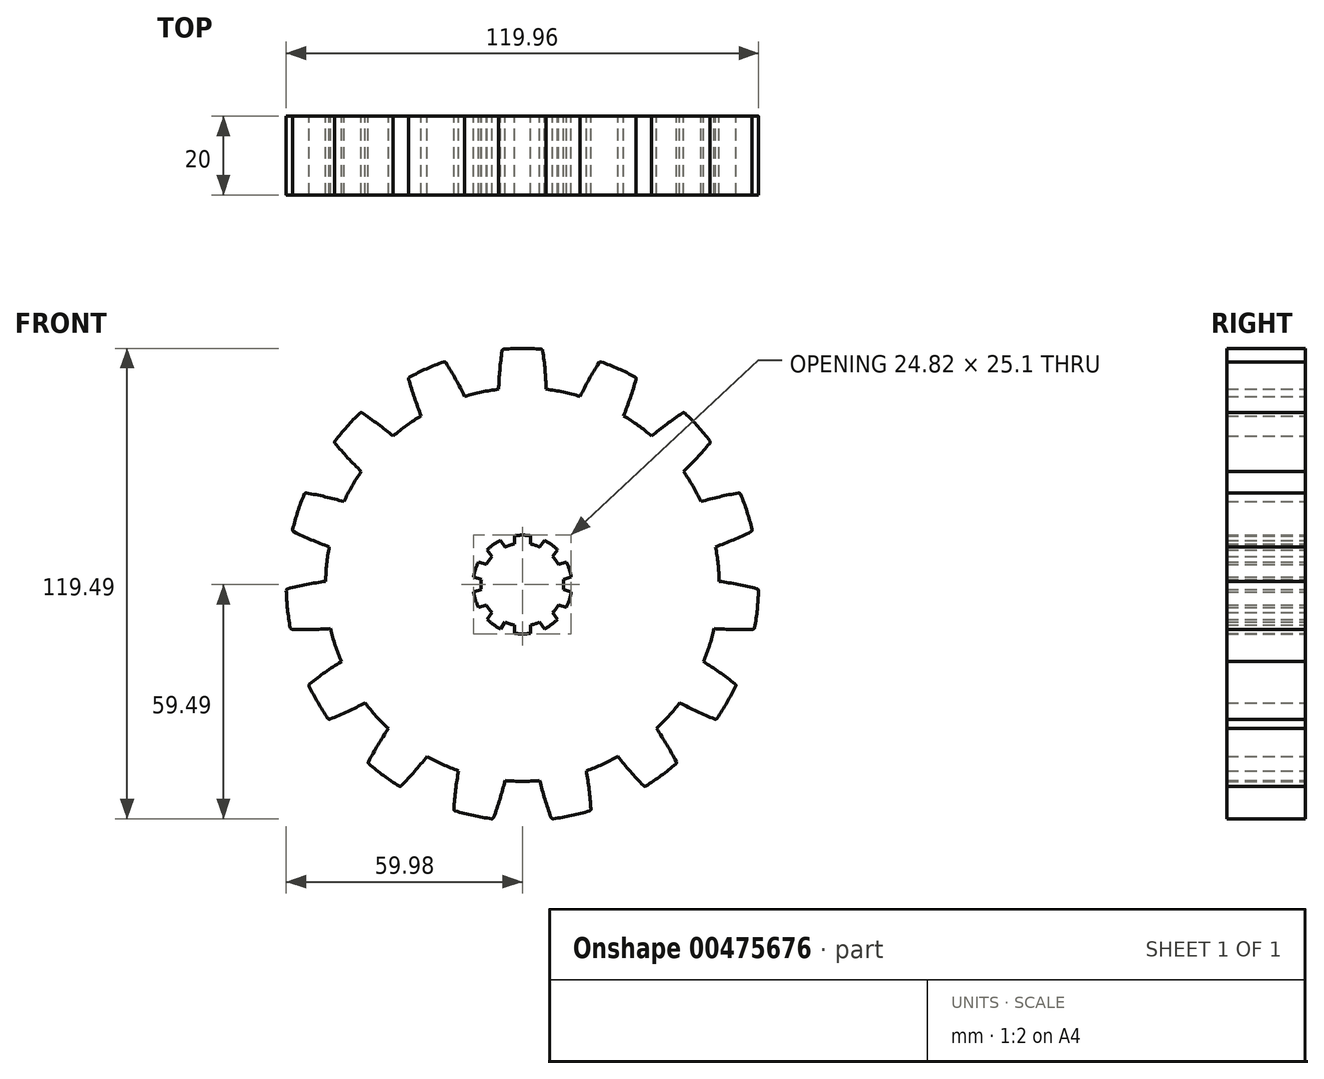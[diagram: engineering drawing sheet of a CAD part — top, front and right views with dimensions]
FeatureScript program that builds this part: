
annotation { "Feature Type Name" : "Feature", "Feature Type Description" : "" }
export const myFeature = defineFeature(function(context is Context, id is Id, definition is map)
    precondition{}
    {
        {
            var Q0;
            Q0=qCreatedBy(makeId("Front.planeOp"),FACE);
            var sketch = newSketch(context, id + "F0", { "sketchPlane" : qUnion([Q0])});
            skArc(sketch, "E0", {"start": v(2.05, 12.38) * mm, "mid": v(0, 12.55) * mm, "end": v(-2.05, 12.38) * mm});
            skArc(sketch, "E1", {"start": v(-10.43, 1.23) * mm, "mid": v(-10.5, 0) * mm, "end": v(-10.43, -1.23) * mm});
            skLineSegment(sketch, "E2.left", {"start": v(2.05, 12.38) * mm, "end": v(2.05, 10.3) * mm});
            skLineSegment(sketch, "E2.right", {"start": v(-2.05, 12.38) * mm, "end": v(-2.05, 10.3) * mm});
            skPoint(sketch, "E3.orphan", {"position": v(-2.05, 12.55) * mm});
            skPoint(sketch, "E4.orphan", {"position": v(2.05, 12.55) * mm});
            skPoint(sketch, "E5.trimOffspring.end.orphan", {"position": v(2.05, -12.55) * mm});
            skPoint(sketch, "E6.trimOffspring.end.orphan", {"position": v(-2.05, -12.55) * mm});
            skLineSegment(sketch, "E7.1.0", {"start": v(-8.94, 8.81) * mm, "end": v(-7.71, 7.13) * mm});
            skArc(sketch, "E7.1.1", {"start": v(-5.62, 11.22) * mm, "mid": v(-7.38, 10.15) * mm, "end": v(-8.94, 8.81) * mm});
            skLineSegment(sketch, "E7.1.2", {"start": v(-5.62, 11.22) * mm, "end": v(-4.4, 9.54) * mm});
            skLineSegment(sketch, "E7.2.0", {"start": v(-12.4, 1.88) * mm, "end": v(-10.43, 1.23) * mm});
            skArc(sketch, "E7.2.1", {"start": v(-11.14, 5.78) * mm, "mid": v(-11.94, 3.88) * mm, "end": v(-12.4, 1.88) * mm});
            skLineSegment(sketch, "E7.2.2", {"start": v(-11.14, 5.78) * mm, "end": v(-9.16, 5.13) * mm});
            skLineSegment(sketch, "E7.3.0", {"start": v(-11.14, -5.78) * mm, "end": v(-9.16, -5.13) * mm});
            skArc(sketch, "E7.3.1", {"start": v(-12.4, -1.88) * mm, "mid": v(-11.94, -3.88) * mm, "end": v(-11.14, -5.78) * mm});
            skLineSegment(sketch, "E7.3.2", {"start": v(-12.4, -1.88) * mm, "end": v(-10.43, -1.23) * mm});
            skLineSegment(sketch, "E7.4.0", {"start": v(-5.62, -11.22) * mm, "end": v(-4.4, -9.54) * mm});
            skArc(sketch, "E7.4.1", {"start": v(-8.94, -8.81) * mm, "mid": v(-7.38, -10.15) * mm, "end": v(-5.62, -11.22) * mm});
            skLineSegment(sketch, "E7.4.2", {"start": v(-8.94, -8.81) * mm, "end": v(-7.71, -7.13) * mm});
            skLineSegment(sketch, "E7.5.0", {"start": v(2.05, -12.38) * mm, "end": v(2.05, -10.3) * mm});
            skArc(sketch, "E7.5.1", {"start": v(-2.05, -12.38) * mm, "mid": v(0, -12.55) * mm, "end": v(2.05, -12.38) * mm});
            skLineSegment(sketch, "E7.5.2", {"start": v(-2.05, -12.38) * mm, "end": v(-2.05, -10.3) * mm});
            skLineSegment(sketch, "E7.6.0", {"start": v(8.94, -8.81) * mm, "end": v(7.71, -7.13) * mm});
            skArc(sketch, "E7.6.1", {"start": v(5.62, -11.22) * mm, "mid": v(7.38, -10.15) * mm, "end": v(8.94, -8.81) * mm});
            skLineSegment(sketch, "E7.6.2", {"start": v(5.62, -11.22) * mm, "end": v(4.4, -9.54) * mm});
            skLineSegment(sketch, "E7.7.0", {"start": v(12.4, -1.88) * mm, "end": v(10.43, -1.23) * mm});
            skArc(sketch, "E7.7.1", {"start": v(11.14, -5.78) * mm, "mid": v(11.94, -3.88) * mm, "end": v(12.4, -1.88) * mm});
            skLineSegment(sketch, "E7.7.2", {"start": v(11.14, -5.78) * mm, "end": v(9.16, -5.13) * mm});
            skLineSegment(sketch, "E7.8.0", {"start": v(11.14, 5.78) * mm, "end": v(9.16, 5.13) * mm});
            skArc(sketch, "E7.8.1", {"start": v(12.4, 1.88) * mm, "mid": v(11.94, 3.88) * mm, "end": v(11.14, 5.78) * mm});
            skLineSegment(sketch, "E7.8.2", {"start": v(12.4, 1.88) * mm, "end": v(10.43, 1.23) * mm});
            skLineSegment(sketch, "E7.9.0", {"start": v(5.62, 11.22) * mm, "end": v(4.4, 9.54) * mm});
            skArc(sketch, "E7.9.1", {"start": v(8.94, 8.81) * mm, "mid": v(7.38, 10.15) * mm, "end": v(5.62, 11.22) * mm});
            skLineSegment(sketch, "E7.9.2", {"start": v(8.94, 8.81) * mm, "end": v(7.71, 7.13) * mm});
            skArc(sketch, "E8.trimOffspring", {"start": v(-7.71, 7.13) * mm, "mid": v(-8.5, 6.17) * mm, "end": v(-9.16, 5.13) * mm});
            skArc(sketch, "E9.trimOffspring", {"start": v(-2.05, 10.3) * mm, "mid": v(-3.24, 9.99) * mm, "end": v(-4.4, 9.54) * mm});
            skArc(sketch, "E10.trimOffspring", {"start": v(4.4, 9.54) * mm, "mid": v(3.24, 9.99) * mm, "end": v(2.05, 10.3) * mm});
            skArc(sketch, "E11.trimOffspring", {"start": v(9.16, 5.13) * mm, "mid": v(8.5, 6.17) * mm, "end": v(7.71, 7.13) * mm});
            skArc(sketch, "E12.trimOffspring", {"start": v(10.43, -1.23) * mm, "mid": v(10.5, 0) * mm, "end": v(10.43, 1.23) * mm});
            skArc(sketch, "E13.trimOffspring", {"start": v(7.71, -7.13) * mm, "mid": v(8.5, -6.17) * mm, "end": v(9.16, -5.13) * mm});
            skArc(sketch, "E14.trimOffspring", {"start": v(2.05, -10.3) * mm, "mid": v(3.24, -9.99) * mm, "end": v(4.4, -9.54) * mm});
            skArc(sketch, "E15.trimOffspring", {"start": v(-4.4, -9.54) * mm, "mid": v(-3.24, -9.99) * mm, "end": v(-2.05, -10.3) * mm});
            skArc(sketch, "E16.trimOffspring", {"start": v(-9.16, -5.13) * mm, "mid": v(-8.5, -6.17) * mm, "end": v(-7.71, -7.13) * mm});
            skArc(sketch, "E17", {"start": v(-5.11, 59.78) * mm, "mid": v(-5.72, 54.72) * mm, "end": v(-6.05, 49.63) * mm});
            skArc(sketch, "E18.trimOffspring", {"start": v(5.11, 59.78) * mm, "mid": v(0, 60) * mm, "end": v(-5.11, 59.78) * mm});
            skArc(sketch, "E19.trimOffspring", {"start": v(6.05, 49.63) * mm, "mid": v(5.72, 54.72) * mm, "end": v(5.11, 59.78) * mm});
            skPoint(sketch, "E20.orphan", {"position": v(0, 46.5) * mm});
            skArc(sketch, "E21.1.0", {"start": v(-14.66, 47.8) * mm, "mid": v(-17.03, 52.32) * mm, "end": v(-19.64, 56.7) * mm});
            skPoint(sketch, "E21.1.1", {"position": v(-18.91, 42.48) * mm});
            skArc(sketch, "E21.1.2", {"start": v(-19.64, 56.7) * mm, "mid": v(-24.4, 54.81) * mm, "end": v(-28.99, 52.53) * mm});
            skArc(sketch, "E21.1.3", {"start": v(-28.99, 52.53) * mm, "mid": v(-27.49, 47.66) * mm, "end": v(-25.71, 42.88) * mm});
            skArc(sketch, "E21.2.0", {"start": v(-32.84, 37.7) * mm, "mid": v(-36.84, 40.87) * mm, "end": v(-41, 43.8) * mm});
            skPoint(sketch, "E21.2.1", {"position": v(-34.56, 31.11) * mm});
            skArc(sketch, "E21.2.2", {"start": v(-41, 43.8) * mm, "mid": v(-44.59, 40.15) * mm, "end": v(-47.85, 36.2) * mm});
            skArc(sketch, "E21.2.3", {"start": v(-47.85, 36.2) * mm, "mid": v(-44.5, 32.36) * mm, "end": v(-40.93, 28.72) * mm});
            skArc(sketch, "E21.3.0", {"start": v(-45.34, 21.09) * mm, "mid": v(-50.27, 22.35) * mm, "end": v(-55.28, 23.34) * mm});
            skPoint(sketch, "E21.3.1", {"position": v(-44.22, 14.37) * mm});
            skArc(sketch, "E21.3.2", {"start": v(-55.28, 23.34) * mm, "mid": v(-57.06, 18.54) * mm, "end": v(-58.44, 13.6) * mm});
            skArc(sketch, "E21.3.3", {"start": v(-58.44, 13.6) * mm, "mid": v(-53.81, 11.47) * mm, "end": v(-49.07, 9.59) * mm});
            skArc(sketch, "E21.4.0", {"start": v(-50, 0.82) * mm, "mid": v(-55.02, -0.03) * mm, "end": v(-59.99, -1.16) * mm});
            skPoint(sketch, "E21.4.1", {"position": v(-46.25, -4.86) * mm});
            skArc(sketch, "E21.4.2", {"start": v(-59.99, -1.16) * mm, "mid": v(-59.67, -6.27) * mm, "end": v(-58.92, -11.34) * mm});
            skArc(sketch, "E21.4.3", {"start": v(-58.92, -11.34) * mm, "mid": v(-53.82, -11.41) * mm, "end": v(-48.73, -11.2) * mm});
            skArc(sketch, "E21.5.0", {"start": v(-46, -19.58) * mm, "mid": v(-50.25, -22.4) * mm, "end": v(-54.33, -25.46) * mm});
            skPoint(sketch, "E21.5.1", {"position": v(-40.27, -23.25) * mm});
            skArc(sketch, "E21.5.2", {"start": v(-54.33, -25.46) * mm, "mid": v(-51.96, -30) * mm, "end": v(-49.22, -34.32) * mm});
            skArc(sketch, "E21.5.3", {"start": v(-49.22, -34.32) * mm, "mid": v(-44.53, -32.32) * mm, "end": v(-39.96, -30.05) * mm});
            skArc(sketch, "E21.6.0", {"start": v(-34.06, -36.6) * mm, "mid": v(-36.8, -40.9) * mm, "end": v(-39.28, -45.36) * mm});
            skPoint(sketch, "E21.6.1", {"position": v(-27.33, -37.62) * mm});
            skArc(sketch, "E21.6.2", {"start": v(-39.28, -45.36) * mm, "mid": v(-35.27, -48.54) * mm, "end": v(-31, -51.37) * mm});
            skArc(sketch, "E21.6.3", {"start": v(-31, -51.37) * mm, "mid": v(-27.53, -47.63) * mm, "end": v(-24.28, -43.7) * mm});
            skArc(sketch, "E21.7.0", {"start": v(-16.23, -47.3) * mm, "mid": v(-16.98, -52.33) * mm, "end": v(-17.43, -57.41) * mm});
            skPoint(sketch, "E21.7.1", {"position": v(-9.67, -45.48) * mm});
            skArc(sketch, "E21.7.2", {"start": v(-17.43, -57.41) * mm, "mid": v(-12.47, -58.69) * mm, "end": v(-7.43, -59.54) * mm});
            skArc(sketch, "E21.7.3", {"start": v(-7.43, -59.54) * mm, "mid": v(-5.78, -54.71) * mm, "end": v(-4.4, -49.8) * mm});
            skArc(sketch, "E21.8.0", {"start": v(4.4, -49.8) * mm, "mid": v(5.78, -54.71) * mm, "end": v(7.43, -59.54) * mm});
            skPoint(sketch, "E21.8.1", {"position": v(9.67, -45.48) * mm});
            skArc(sketch, "E21.8.2", {"start": v(7.43, -59.54) * mm, "mid": v(12.47, -58.69) * mm, "end": v(17.43, -57.41) * mm});
            skArc(sketch, "E21.8.3", {"start": v(17.43, -57.41) * mm, "mid": v(16.98, -52.33) * mm, "end": v(16.23, -47.3) * mm});
            skArc(sketch, "E21.9.0", {"start": v(24.28, -43.7) * mm, "mid": v(27.53, -47.63) * mm, "end": v(31, -51.37) * mm});
            skPoint(sketch, "E21.9.1", {"position": v(27.33, -37.62) * mm});
            skArc(sketch, "E21.9.2", {"start": v(31, -51.37) * mm, "mid": v(35.27, -48.54) * mm, "end": v(39.28, -45.36) * mm});
            skArc(sketch, "E21.9.3", {"start": v(39.28, -45.36) * mm, "mid": v(36.8, -40.9) * mm, "end": v(34.06, -36.6) * mm});
            skArc(sketch, "E21.10.0", {"start": v(39.96, -30.05) * mm, "mid": v(44.53, -32.32) * mm, "end": v(49.22, -34.32) * mm});
            skPoint(sketch, "E21.10.1", {"position": v(40.27, -23.25) * mm});
            skArc(sketch, "E21.10.2", {"start": v(49.22, -34.32) * mm, "mid": v(51.96, -30) * mm, "end": v(54.33, -25.46) * mm});
            skArc(sketch, "E21.10.3", {"start": v(54.33, -25.46) * mm, "mid": v(50.25, -22.4) * mm, "end": v(46, -19.58) * mm});
            skArc(sketch, "E21.11.0", {"start": v(48.73, -11.2) * mm, "mid": v(53.82, -11.41) * mm, "end": v(58.92, -11.34) * mm});
            skPoint(sketch, "E21.11.1", {"position": v(46.25, -4.86) * mm});
            skArc(sketch, "E21.11.2", {"start": v(58.92, -11.34) * mm, "mid": v(59.67, -6.27) * mm, "end": v(59.99, -1.16) * mm});
            skArc(sketch, "E21.11.3", {"start": v(59.99, -1.16) * mm, "mid": v(55.02, -0.03) * mm, "end": v(50, 0.82) * mm});
            skArc(sketch, "E21.12.0", {"start": v(49.07, 9.59) * mm, "mid": v(53.81, 11.47) * mm, "end": v(58.44, 13.6) * mm});
            skPoint(sketch, "E21.12.1", {"position": v(44.22, 14.37) * mm});
            skArc(sketch, "E21.12.2", {"start": v(58.44, 13.6) * mm, "mid": v(57.06, 18.54) * mm, "end": v(55.28, 23.34) * mm});
            skArc(sketch, "E21.12.3", {"start": v(55.28, 23.34) * mm, "mid": v(50.27, 22.35) * mm, "end": v(45.34, 21.09) * mm});
            skArc(sketch, "E21.13.0", {"start": v(40.93, 28.72) * mm, "mid": v(44.5, 32.36) * mm, "end": v(47.85, 36.2) * mm});
            skPoint(sketch, "E21.13.1", {"position": v(34.56, 31.11) * mm});
            skArc(sketch, "E21.13.2", {"start": v(47.85, 36.2) * mm, "mid": v(44.59, 40.15) * mm, "end": v(41, 43.8) * mm});
            skArc(sketch, "E21.13.3", {"start": v(41, 43.8) * mm, "mid": v(36.84, 40.87) * mm, "end": v(32.84, 37.7) * mm});
            skArc(sketch, "E21.14.0", {"start": v(25.71, 42.88) * mm, "mid": v(27.49, 47.66) * mm, "end": v(28.99, 52.53) * mm});
            skPoint(sketch, "E21.14.1", {"position": v(18.91, 42.48) * mm});
            skArc(sketch, "E21.14.2", {"start": v(28.99, 52.53) * mm, "mid": v(24.4, 54.81) * mm, "end": v(19.64, 56.7) * mm});
            skArc(sketch, "E21.14.3", {"start": v(19.64, 56.7) * mm, "mid": v(17.03, 52.32) * mm, "end": v(14.66, 47.8) * mm});
            skArc(sketch, "E22", {"start": v(34.06, -36.6) * mm, "mid": v(37.16, -33.46) * mm, "end": v(39.96, -30.05) * mm});
            skArc(sketch, "E23.trimOffspring", {"start": v(16.23, -47.3) * mm, "mid": v(20.34, -45.68) * mm, "end": v(24.28, -43.7) * mm});
            skArc(sketch, "E24.trimOffspring", {"start": v(-4.4, -49.8) * mm, "mid": v(0, -50) * mm, "end": v(4.4, -49.8) * mm});
            skArc(sketch, "E25.trimOffspring", {"start": v(-24.28, -43.7) * mm, "mid": v(-20.34, -45.68) * mm, "end": v(-16.23, -47.3) * mm});
            skArc(sketch, "E26.trimOffspring", {"start": v(-39.96, -30.05) * mm, "mid": v(-37.16, -33.46) * mm, "end": v(-34.06, -36.6) * mm});
            skArc(sketch, "E27.trimOffspring", {"start": v(-48.73, -11.2) * mm, "mid": v(-47.55, -15.45) * mm, "end": v(-46, -19.58) * mm});
            skArc(sketch, "E28.trimOffspring", {"start": v(-49.07, 9.59) * mm, "mid": v(-49.73, 5.23) * mm, "end": v(-50, 0.82) * mm});
            skArc(sketch, "E29.trimOffspring", {"start": v(-40.93, 28.72) * mm, "mid": v(-43.3, 25) * mm, "end": v(-45.34, 21.09) * mm});
            skArc(sketch, "E30.trimOffspring", {"start": v(-25.71, 42.88) * mm, "mid": v(-29.39, 40.45) * mm, "end": v(-32.84, 37.7) * mm});
            skArc(sketch, "E31.trimOffspring", {"start": v(-6.05, 49.63) * mm, "mid": v(-10.4, 48.9) * mm, "end": v(-14.66, 47.8) * mm});
            skArc(sketch, "E32.trimOffspring", {"start": v(14.66, 47.8) * mm, "mid": v(10.4, 48.9) * mm, "end": v(6.05, 49.63) * mm});
            skArc(sketch, "E33.trimOffspring", {"start": v(32.84, 37.7) * mm, "mid": v(29.39, 40.45) * mm, "end": v(25.71, 42.88) * mm});
            skArc(sketch, "E34.trimOffspring", {"start": v(45.34, 21.09) * mm, "mid": v(43.3, 25) * mm, "end": v(40.93, 28.72) * mm});
            skArc(sketch, "E35.trimOffspring", {"start": v(50, 0.82) * mm, "mid": v(49.73, 5.23) * mm, "end": v(49.07, 9.59) * mm});
            skArc(sketch, "E36.trimOffspring", {"start": v(46, -19.58) * mm, "mid": v(47.55, -15.45) * mm, "end": v(48.73, -11.2) * mm});
            skSolve(sketch);
        }
        {
            var Q0;
            Q0 = qSketchRegion(id + "F0", true);
            extrude(context, id + "F1", {"entities" : qUnion([Q0]), "depth" : 20 * mm});
        }
        {
            var Q0;
            Q0=makeQuery(id+"F1.opExtrude","SWEPT_EDGE",EDGE,{"disambiguationData":[OSD([sQuery(id+"F0.wireOp",EDGE,"E17"),sQuery(id+"F0.wireOp",EDGE,"E18.trimOffspring")])]});
            var Q1;
            Q1=makeQuery(id+"F1.opExtrude","SWEPT_EDGE",EDGE,{"disambiguationData":[OSD([sQuery(id+"F0.wireOp",EDGE,"E18.trimOffspring"),sQuery(id+"F0.wireOp",EDGE,"E19.trimOffspring")])]});
            var Q2;
            Q2=makeQuery(id+"F1.opExtrude","SWEPT_EDGE",EDGE,{"disambiguationData":[OSD([sQuery(id+"F0.wireOp",EDGE,"E21.14.2"),sQuery(id+"F0.wireOp",EDGE,"E21.14.3")])]});
            var Q3;
            Q3=makeQuery(id+"F1.opExtrude","SWEPT_EDGE",EDGE,{"disambiguationData":[OSD([sQuery(id+"F0.wireOp",EDGE,"E21.14.0"),sQuery(id+"F0.wireOp",EDGE,"E21.14.2")])]});
            var Q4;
            Q4=makeQuery(id+"F1.opExtrude","SWEPT_EDGE",EDGE,{"disambiguationData":[OSD([sQuery(id+"F0.wireOp",EDGE,"E21.13.2"),sQuery(id+"F0.wireOp",EDGE,"E21.13.3")])]});
            var Q5;
            Q5=makeQuery(id+"F1.opExtrude","SWEPT_EDGE",EDGE,{"disambiguationData":[OSD([sQuery(id+"F0.wireOp",EDGE,"E21.13.0"),sQuery(id+"F0.wireOp",EDGE,"E21.13.2")])]});
            var Q6;
            Q6=makeQuery(id+"F1.opExtrude","SWEPT_EDGE",EDGE,{"disambiguationData":[OSD([sQuery(id+"F0.wireOp",EDGE,"E21.12.2"),sQuery(id+"F0.wireOp",EDGE,"E21.12.3")])]});
            var Q7;
            Q7=makeQuery(id+"F1.opExtrude","SWEPT_EDGE",EDGE,{"disambiguationData":[OSD([sQuery(id+"F0.wireOp",EDGE,"E21.12.0"),sQuery(id+"F0.wireOp",EDGE,"E21.12.2")])]});
            var Q8;
            Q8=makeQuery(id+"F1.opExtrude","SWEPT_EDGE",EDGE,{"disambiguationData":[OSD([sQuery(id+"F0.wireOp",EDGE,"E21.11.2"),sQuery(id+"F0.wireOp",EDGE,"E21.11.3")])]});
            var Q9;
            Q9=makeQuery(id+"F1.opExtrude","SWEPT_EDGE",EDGE,{"disambiguationData":[OSD([sQuery(id+"F0.wireOp",EDGE,"E21.11.0"),sQuery(id+"F0.wireOp",EDGE,"E21.11.2")])]});
            var Q10;
            Q10=makeQuery(id+"F1.opExtrude","SWEPT_EDGE",EDGE,{"disambiguationData":[OSD([sQuery(id+"F0.wireOp",EDGE,"E21.10.2"),sQuery(id+"F0.wireOp",EDGE,"E21.10.3")])]});
            var Q11;
            Q11=makeQuery(id+"F1.opExtrude","SWEPT_EDGE",EDGE,{"disambiguationData":[OSD([sQuery(id+"F0.wireOp",EDGE,"E21.10.0"),sQuery(id+"F0.wireOp",EDGE,"E21.10.2")])]});
            var Q12;
            Q12=makeQuery(id+"F1.opExtrude","SWEPT_EDGE",EDGE,{"disambiguationData":[OSD([sQuery(id+"F0.wireOp",EDGE,"E21.9.2"),sQuery(id+"F0.wireOp",EDGE,"E21.9.3")])]});
            var Q13;
            Q13=makeQuery(id+"F1.opExtrude","SWEPT_EDGE",EDGE,{"disambiguationData":[OSD([sQuery(id+"F0.wireOp",EDGE,"E21.9.0"),sQuery(id+"F0.wireOp",EDGE,"E21.9.2")])]});
            var Q14;
            Q14=makeQuery(id+"F1.opExtrude","SWEPT_EDGE",EDGE,{"disambiguationData":[OSD([sQuery(id+"F0.wireOp",EDGE,"E21.8.2"),sQuery(id+"F0.wireOp",EDGE,"E21.8.3")])]});
            var Q15;
            Q15=makeQuery(id+"F1.opExtrude","SWEPT_EDGE",EDGE,{"disambiguationData":[OSD([sQuery(id+"F0.wireOp",EDGE,"E21.8.0"),sQuery(id+"F0.wireOp",EDGE,"E21.8.2")])]});
            var Q16;
            Q16=makeQuery(id+"F1.opExtrude","SWEPT_EDGE",EDGE,{"disambiguationData":[OSD([sQuery(id+"F0.wireOp",EDGE,"E21.7.2"),sQuery(id+"F0.wireOp",EDGE,"E21.7.3")])]});
            var Q17;
            Q17=makeQuery(id+"F1.opExtrude","SWEPT_EDGE",EDGE,{"disambiguationData":[OSD([sQuery(id+"F0.wireOp",EDGE,"E21.7.0"),sQuery(id+"F0.wireOp",EDGE,"E21.7.2")])]});
            var Q18;
            Q18=makeQuery(id+"F1.opExtrude","SWEPT_EDGE",EDGE,{"disambiguationData":[OSD([sQuery(id+"F0.wireOp",EDGE,"E21.6.0"),sQuery(id+"F0.wireOp",EDGE,"E21.6.2")])]});
            var Q19;
            Q19=makeQuery(id+"F1.opExtrude","SWEPT_EDGE",EDGE,{"disambiguationData":[OSD([sQuery(id+"F0.wireOp",EDGE,"E21.6.2"),sQuery(id+"F0.wireOp",EDGE,"E21.6.3")])]});
            var Q20;
            Q20=makeQuery(id+"F1.opExtrude","SWEPT_EDGE",EDGE,{"disambiguationData":[OSD([sQuery(id+"F0.wireOp",EDGE,"E21.5.0"),sQuery(id+"F0.wireOp",EDGE,"E21.5.2")])]});
            var Q21;
            Q21=makeQuery(id+"F1.opExtrude","SWEPT_EDGE",EDGE,{"disambiguationData":[OSD([sQuery(id+"F0.wireOp",EDGE,"E21.5.2"),sQuery(id+"F0.wireOp",EDGE,"E21.5.3")])]});
            var Q22;
            Q22=makeQuery(id+"F1.opExtrude","SWEPT_EDGE",EDGE,{"disambiguationData":[OSD([sQuery(id+"F0.wireOp",EDGE,"E21.4.0"),sQuery(id+"F0.wireOp",EDGE,"E21.4.2")])]});
            var Q23;
            Q23=makeQuery(id+"F1.opExtrude","SWEPT_EDGE",EDGE,{"disambiguationData":[OSD([sQuery(id+"F0.wireOp",EDGE,"E21.4.2"),sQuery(id+"F0.wireOp",EDGE,"E21.4.3")])]});
            var Q24;
            Q24=makeQuery(id+"F1.opExtrude","SWEPT_EDGE",EDGE,{"disambiguationData":[OSD([sQuery(id+"F0.wireOp",EDGE,"E21.3.0"),sQuery(id+"F0.wireOp",EDGE,"E21.3.2")])]});
            var Q25;
            Q25=makeQuery(id+"F1.opExtrude","SWEPT_EDGE",EDGE,{"disambiguationData":[OSD([sQuery(id+"F0.wireOp",EDGE,"E21.3.2"),sQuery(id+"F0.wireOp",EDGE,"E21.3.3")])]});
            var Q26;
            Q26=makeQuery(id+"F1.opExtrude","SWEPT_EDGE",EDGE,{"disambiguationData":[OSD([sQuery(id+"F0.wireOp",EDGE,"E21.2.0"),sQuery(id+"F0.wireOp",EDGE,"E21.2.2")])]});
            var Q27;
            Q27=makeQuery(id+"F1.opExtrude","SWEPT_EDGE",EDGE,{"disambiguationData":[OSD([sQuery(id+"F0.wireOp",EDGE,"E21.2.2"),sQuery(id+"F0.wireOp",EDGE,"E21.2.3")])]});
            var Q28;
            Q28=makeQuery(id+"F1.opExtrude","SWEPT_EDGE",EDGE,{"disambiguationData":[OSD([sQuery(id+"F0.wireOp",EDGE,"E21.1.0"),sQuery(id+"F0.wireOp",EDGE,"E21.1.2")])]});
            var Q29;
            Q29=makeQuery(id+"F1.opExtrude","SWEPT_EDGE",EDGE,{"disambiguationData":[OSD([sQuery(id+"F0.wireOp",EDGE,"E21.1.2"),sQuery(id+"F0.wireOp",EDGE,"E21.1.3")])]});
            fillet(context, id + "F2", {"entities" : qUnion([Q0, Q1, Q2, Q3, Q4, Q5, Q6, Q7, Q8, Q9, Q10, Q11, Q12, Q13, Q14, Q15, Q16, Q17, Q18, Q19, Q20, Q21, Q22, Q23, Q24, Q25, Q26, Q27, Q28, Q29]), "radius" : 0.5 * mm, "tangentPropagation" : true, "allowEdgeOverflow" : false});
        }
    });
